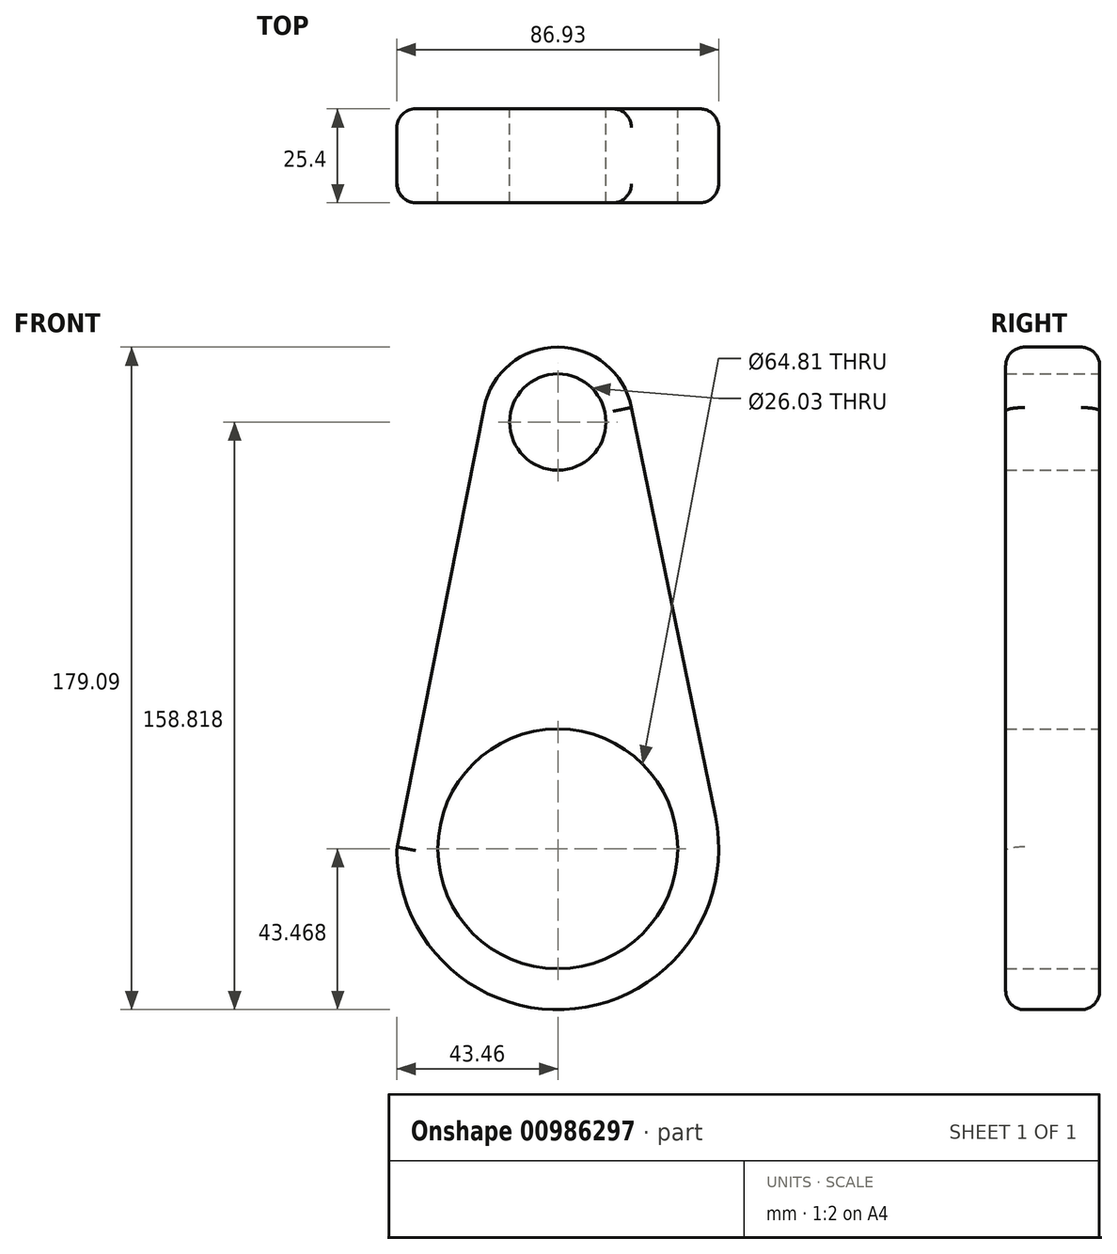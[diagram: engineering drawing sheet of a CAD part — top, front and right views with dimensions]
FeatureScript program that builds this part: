
annotation { "Feature Type Name" : "Feature", "Feature Type Description" : "" }
export const myFeature = defineFeature(function(context is Context, id is Id, definition is map)
    precondition{}
    {
        {
            var Q0;
            Q0=qCreatedBy(makeId("Front.planeOp"),FACE);
            var sketch = newSketch(context, id + "F0", { "sketchPlane" : qUnion([Q0])});
            skArc(sketch, "E0", {"start": v(-40.2, -39.12) * mm, "mid": v(-4.08, -98.94) * mm, "end": v(42.58, -46.92) * mm});
            skArc(sketch, "E1", {"start": v(19.88, 63.62) * mm, "mid": v(0, 79.96) * mm, "end": v(-19.88, 63.62) * mm});
            skLineSegment(sketch, "E2", {"start": v(-43.47, -55.66) * mm, "end": v(-19.88, 63.62) * mm});
            skLineSegment(sketch, "E3", {"start": v(19.88, 63.62) * mm, "end": v(44.37, -55.66) * mm});
            skCircle(sketch, "E4", {"center": v(0, 59.69) * mm, "radius": 13.01 * mm});
            skCircle(sketch, "E5", {"center": v(0, -55.66) * mm, "radius": 32.4 * mm});
            skSolve(sketch);
        }
        {
            var Q0;
            {var subQ3=sQuery(id+"F0.wireOp",EDGE,"E1");Q0=makeQuery(id+"F0.imprint","IMPRINT",FACE,{"disambiguationData":[TD([[makeQuery(id+"F0.imprint","IMPRINT",EDGE,{"derivedFrom":subQ3}),1.0]])]});}
            extrude(context, id + "F1", {"entities" : qUnion([Q0]), "depth" : 25.4 * mm, "offsetDistance" : 25.4 * mm});
        }
        {
            var Q0;
            Q0=makeQuery(id+"F1.opExtrude","CAP_EDGE",EDGE,{"disambiguationData":[OSD([sQuery(id+"F0.wireOp",EDGE,"E2")])],"isStart":false});
            fillet(context, id + "F2", {"entities" : qUnion([Q0]), "radius" : 5.08 * mm, "tangentPropagation" : true, "allowEdgeOverflow" : false});
        }
        {
            var Q0;
            Q0=makeQuery(id+"F1.opExtrude","CAP_EDGE",EDGE,{"disambiguationData":[OSD([sQuery(id+"F0.wireOp",EDGE,"E0")])],"isStart":false});
            fillet(context, id + "F3", {"entities" : qUnion([Q0]), "radius" : 5.08 * mm, "tangentPropagation" : true, "allowEdgeOverflow" : false});
        }
        {
            var Q0;
            Q0=makeQuery(id+"F1.opExtrude","CAP_EDGE",EDGE,{"disambiguationData":[OSD([sQuery(id+"F0.wireOp",EDGE,"E3")])],"isStart":true});
            fillet(context, id + "F4", {"entities" : qUnion([Q0]), "radius" : 5.08 * mm, "tangentPropagation" : true, "allowEdgeOverflow" : false});
        }
    });
